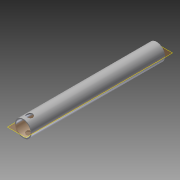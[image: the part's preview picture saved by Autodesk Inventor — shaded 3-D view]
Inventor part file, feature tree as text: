
AUTODESK INVENTOR PART (.ipt)
format: ipt  version: 2014 (Build 180170000, 170)  size: 88,064 bytes
history: native  units: in
note: dims shown in document units (in); Inventor stores cm internally (conversion verified against a paired STEP export)
features: extrude x2, sketch x2
ambient origin geometry x8: Origin, YZ Plane, XZ Plane, XY Plane, X Axis, Y Axis, Z Axis, Center Point
bodies: Solid1 (feature_tree)
feature tree (4):
  extrude  "Extrusion1"  Depth=0.875in
  extrude  "Extrusion2"  Depth=7.875in
  sketch  "Sketch1"  dims[d0=1.0in d1=0.875in]
  sketch  "Sketch2"  dims[d2=8.25in d3=0.0in d4=0.375in d5=7.875in d6=1.0in d7=0.0in]
